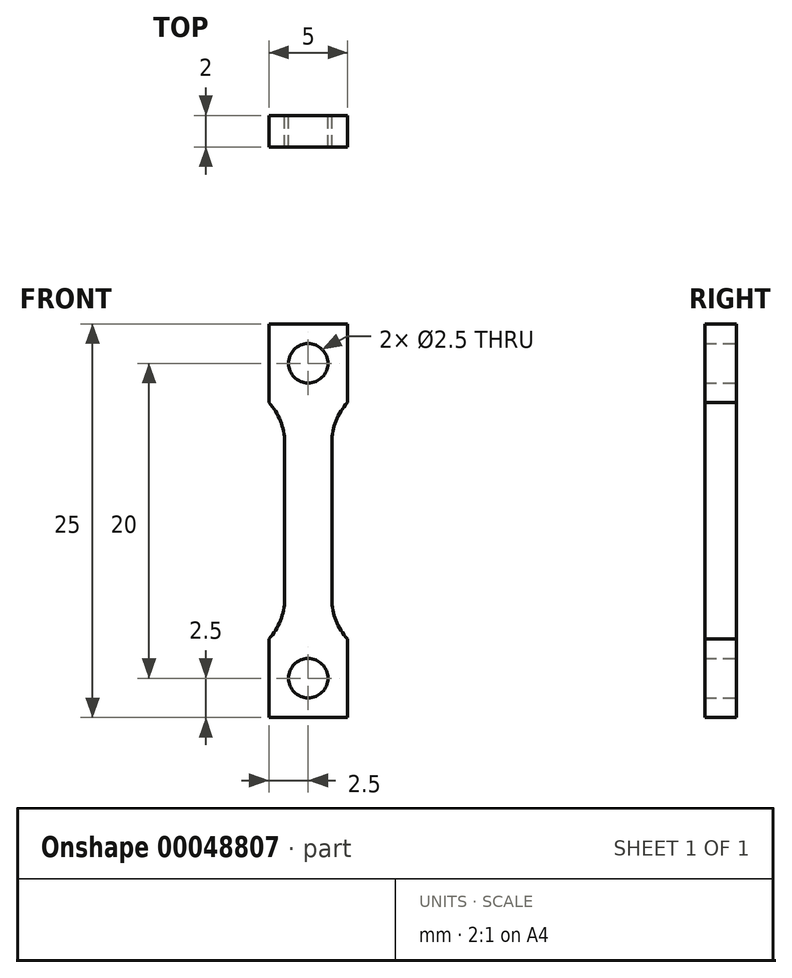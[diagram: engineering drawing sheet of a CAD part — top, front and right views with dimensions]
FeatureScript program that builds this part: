
annotation { "Feature Type Name" : "Feature", "Feature Type Description" : "" }
export const myFeature = defineFeature(function(context is Context, id is Id, definition is map)
    precondition{}
    {
        {
            var Q0;
            Q0=qCreatedBy(makeId("Front.planeOp"),FACE);
            var sketch = newSketch(context, id + "F0", { "sketchPlane" : qUnion([Q0])});
            skPoint(sketch, "E0.middle", {"position": v(0, 0) * mm});
            skLineSegment(sketch, "E1", {"start": v(1.5, 0) * mm, "end": v(1.5, 5) * mm});
            skLineSegment(sketch, "E2", {"start": v(2.5, 12.5) * mm, "end": v(2.5, 7.5) * mm});
            skArc(sketch, "E3", {"start": v(1.5, 5) * mm, "mid": v(1.76, 6.35) * mm, "end": v(2.5, 7.5) * mm});
            skLineSegment(sketch, "E4", {"start": v(2.5, 12.5) * mm, "end": v(0, 12.5) * mm});
            skLineSegment(sketch, "E5.MirrorCS", {"start": v(-2.5, 12.5) * mm, "end": v(0, 12.5) * mm});
            skLineSegment(sketch, "E6.MirrorCS", {"start": v(-2.5, 12.5) * mm, "end": v(-2.5, 7.5) * mm});
            skArc(sketch, "E7.MirrorCS", {"start": v(-1.5, 5) * mm, "mid": v(-1.76, 6.35) * mm, "end": v(-2.5, 7.5) * mm});
            skLineSegment(sketch, "E8.MirrorCS", {"start": v(-1.5, 0) * mm, "end": v(-1.5, 5) * mm});
            skLineSegment(sketch, "E9.MirrorCS", {"start": v(1.5, 0) * mm, "end": v(1.5, -5) * mm});
            skArc(sketch, "E10.MirrorCS", {"start": v(1.5, -5) * mm, "mid": v(1.76, -6.35) * mm, "end": v(2.5, -7.5) * mm});
            skLineSegment(sketch, "E11.MirrorCS", {"start": v(2.5, -12.5) * mm, "end": v(2.5, -7.5) * mm});
            skLineSegment(sketch, "E12.MirrorCS", {"start": v(2.5, -12.5) * mm, "end": v(0, -12.5) * mm});
            skLineSegment(sketch, "E13.MirrorCS", {"start": v(-2.5, -12.5) * mm, "end": v(0, -12.5) * mm});
            skLineSegment(sketch, "E14.MirrorCS", {"start": v(-2.5, -12.5) * mm, "end": v(-2.5, -7.5) * mm});
            skArc(sketch, "E15.MirrorCS", {"start": v(-1.5, -5) * mm, "mid": v(-1.76, -6.35) * mm, "end": v(-2.5, -7.5) * mm});
            skLineSegment(sketch, "E16.MirrorCS", {"start": v(-1.5, 0) * mm, "end": v(-1.5, -5) * mm});
            skPoint(sketch, "E17", {"position": v(0, 10) * mm});
            skCircle(sketch, "E18", {"center": v(0, 10) * mm, "radius": 1.25 * mm});
            skCircle(sketch, "E19.MirrorC", {"center": v(0, -10) * mm, "radius": 1.25 * mm});
            skSolve(sketch);
        }
        {
            var Q0;
            Q0=makeQuery(id+"F0.imprint","IMPRINT",FACE,{"disambiguationData":[TD([[makeQuery(id+"F0.imprint","IMPRINT",EDGE,{"derivedFrom":sQuery(id+"F0.wireOp",EDGE,"E1")}),1.0]])]});
            extrude(context, id + "F1", {"entities" : qUnion([Q0]), "depth" : 2 * mm, "symmetric" : true});
        }
    });
